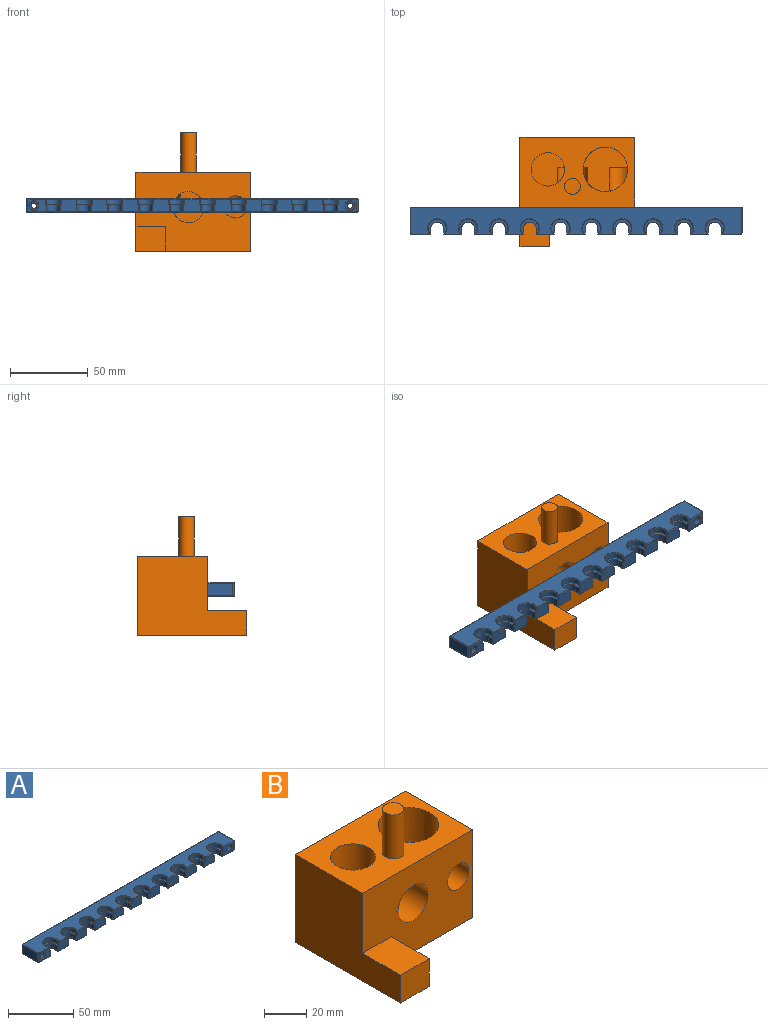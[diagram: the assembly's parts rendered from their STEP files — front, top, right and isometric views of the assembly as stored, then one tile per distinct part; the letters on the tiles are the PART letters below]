
ASSEMBLY  parts=2 mates=1
PART A: 230 faces, bbox 213.6x17.9x8.9 mm
  f0: plane 212.34x16.76mm, normal (0,0,1), area 2525.2mm2, adj f109,f110,f113,f114,f117,f118,f121,f122
  f1: plane 212.34x16.76mm, normal (0,0,-1), area 2906mm2, adj f153,f154,f156,f157,f158,f159,f161,f162
  f2: cylinder r=1.65mm len=9.91mm, axis (0,-1,0), area 102.8mm2, adj f47,f228
  f3: cylinder r=1.65mm len=9.91mm, axis (0,-1,0), area 102.8mm2, adj f47,f229
  f4: plane 4.57x3.56mm, normal (-1,0,0), area 16.3mm2, adj f5,f67,f106,f194
  f5: cylinder r=4.06mm len=8.13mm, axis (0,0,1), area 58.4mm2, adj f4,f6,f67,f192
  f6: plane 4.57x3.56mm, normal (1,0,0), area 16.3mm2, adj f5,f67,f107,f190
  f7: plane 4.57x3.56mm, normal (-1,0,0), area 16.3mm2, adj f8,f65,f104,f182
  f8: cylinder r=4.06mm len=8.13mm, axis (0,0,1), area 58.4mm2, adj f7,f9,f65,f180
  f9: plane 4.57x3.56mm, normal (1,0,0), area 16.3mm2, adj f8,f65,f105,f178
  f10: plane 4.57x3.56mm, normal (-1,0,0), area 16.3mm2, adj f11,f63,f102,f170
  f11: cylinder r=4.06mm len=8.13mm, axis (0,0,1), area 58.4mm2, adj f10,f12,f63,f168
  f12: plane 4.57x3.56mm, normal (1,0,0), area 16.3mm2, adj f11,f63,f103,f166
  f13: plane 4.57x3.56mm, normal (-1,0,0), area 16.3mm2, adj f14,f61,f100,f158
  f14: cylinder r=4.06mm len=8.13mm, axis (0,0,1), area 58.4mm2, adj f13,f15,f61,f156
  f15: plane 4.57x3.56mm, normal (1,0,0), area 16.3mm2, adj f14,f61,f101,f154
  f16: plane 4.57x3.56mm, normal (-1,0,0), area 16.3mm2, adj f17,f59,f98,f157
  f17: cylinder r=4.06mm len=8.13mm, axis (0,0,1), area 58.4mm2, adj f16,f18,f59,f159
  f18: plane 4.57x3.56mm, normal (1,0,0), area 16.3mm2, adj f17,f59,f99,f161
  f19: plane 4.57x3.56mm, normal (-1,0,0), area 16.3mm2, adj f20,f57,f96,f169
  f20: cylinder r=4.06mm len=8.13mm, axis (0,0,1), area 58.4mm2, adj f19,f21,f57,f171
  f21: plane 4.57x3.56mm, normal (1,0,0), area 16.3mm2, adj f20,f57,f97,f173
  f22: plane 4.57x3.56mm, normal (-1,0,0), area 16.3mm2, adj f23,f55,f94,f181
  f23: cylinder r=4.06mm len=8.13mm, axis (0,0,1), area 58.4mm2, adj f22,f24,f55,f183
  f24: plane 4.57x3.56mm, normal (1,0,0), area 16.3mm2, adj f23,f55,f95,f185
  f25: plane 4.57x3.56mm, normal (-1,0,0), area 16.3mm2, adj f26,f53,f92,f193
  f26: cylinder r=4.06mm len=8.13mm, axis (0,0,1), area 58.4mm2, adj f25,f27,f53,f195
  f27: plane 4.57x3.56mm, normal (1,0,0), area 16.3mm2, adj f26,f53,f93,f197
  f28: plane 4.57x3.56mm, normal (-1,0,0), area 16.3mm2, adj f29,f51,f90,f205
  f29: cylinder r=4.06mm len=8.13mm, axis (0,0,1), area 58.4mm2, adj f28,f30,f51,f207
  f30: plane 4.57x3.56mm, normal (1,0,0), area 16.3mm2, adj f29,f51,f91,f209
  f31: plane 4.57x3.56mm, normal (-1,0,0), area 16.3mm2, adj f32,f49,f88,f214
  f32: cylinder r=4.06mm len=8.13mm, axis (0,0,1), area 58.4mm2, adj f31,f33,f49,f212
  f33: plane 4.57x3.56mm, normal (1,0,0), area 16.3mm2, adj f32,f49,f89,f210
  f34: plane 10.67x7.87mm, normal (0,-1,0), area 80.2mm2, adj f49,f51,f85,f86,f88,f91,f134,f213
  f35: plane 10.67x7.87mm, normal (0,-1,0), area 80.2mm2, adj f51,f53,f83,f84,f90,f93,f126,f201
  f36: plane 10.67x7.87mm, normal (0,-1,0), area 80.2mm2, adj f53,f55,f81,f82,f92,f95,f118,f189
  f37: plane 10.67x7.87mm, normal (0,-1,0), area 80.2mm2, adj f55,f57,f79,f80,f94,f97,f110,f177
  f38: plane 10.67x7.87mm, normal (0,-1,0), area 80.2mm2, adj f57,f59,f77,f78,f96,f99,f113,f165
  f39: plane 10.67x7.87mm, normal (0,-1,0), area 80.2mm2, adj f59,f61,f75,f76,f98,f101,f121,f153
  f40: plane 10.67x7.87mm, normal (0,-1,0), area 80.2mm2, adj f61,f63,f73,f74,f100,f103,f129,f162
  f41: plane 10.67x7.87mm, normal (0,-1,0), area 80.2mm2, adj f63,f65,f71,f72,f102,f105,f137,f174
  f42: plane 10.67x7.87mm, normal (0,-1,0), area 80.2mm2, adj f65,f67,f69,f70,f104,f107,f145,f186
  f43: plane 11.68x7.87mm, normal (0,-1,0), area 58.4mm2, adj f67,f68,f106,f150,f198,f221,f223
  f44: plane 16.51x7.87mm, normal (-1,0,0), area 130mm2, adj f47,f144,f204,f226
  f45: plane 11.68x7.87mm, normal (0,-1,0), area 58.4mm2, adj f49,f87,f89,f142,f206,f220,f226
  f46: plane 16.51x7.87mm, normal (1,0,0), area 130mm2, adj f47,f148,f200,f223
  f47: plane 213.36x7.87mm, normal (0,1,0), area 1662.9mm2, adj f2,f3,f44,f46,f146,f202
  f48: cylinder r=5.75mm len=11.49mm, axis (0,0,1), area 82.6mm2, adj f49,f86,f87,f138
  f49: plane 11.49x9.81mm, normal (0,0,1), area 35.7mm2, adj f31,f32,f33,f34,f45,f48,f86,f87
  f50: cylinder r=5.75mm len=11.49mm, axis (0,0,1), area 82.6mm2, adj f51,f84,f85,f130
  f51: plane 11.49x9.81mm, normal (0,0,1), area 35.7mm2, adj f28,f29,f30,f34,f35,f50,f84,f85
  f52: cylinder r=5.75mm len=11.49mm, axis (0,0,1), area 82.6mm2, adj f53,f82,f83,f122
  f53: plane 11.49x9.81mm, normal (0,0,1), area 35.7mm2, adj f25,f26,f27,f35,f36,f52,f82,f83
  f54: cylinder r=5.75mm len=11.49mm, axis (0,0,1), area 82.6mm2, adj f55,f80,f81,f114
  f55: plane 11.49x9.81mm, normal (0,0,1), area 35.7mm2, adj f22,f23,f24,f36,f37,f54,f80,f81
  f56: cylinder r=5.75mm len=11.49mm, axis (0,0,1), area 82.6mm2, adj f57,f78,f79,f109
  f57: plane 11.49x9.81mm, normal (0,0,1), area 35.7mm2, adj f19,f20,f21,f37,f38,f56,f78,f79
  f58: cylinder r=5.75mm len=11.49mm, axis (0,0,1), area 82.6mm2, adj f59,f76,f77,f117
  f59: plane 11.49x9.81mm, normal (0,0,1), area 35.7mm2, adj f16,f17,f18,f38,f39,f58,f76,f77
  f60: cylinder r=5.75mm len=11.49mm, axis (0,0,1), area 82.6mm2, adj f61,f74,f75,f125
  f61: plane 11.49x9.81mm, normal (0,0,1), area 35.7mm2, adj f13,f14,f15,f39,f40,f60,f74,f75
  f62: cylinder r=5.75mm len=11.49mm, axis (0,0,1), area 82.6mm2, adj f63,f72,f73,f133
  f63: plane 11.49x9.81mm, normal (0,0,1), area 35.7mm2, adj f10,f11,f12,f40,f41,f62,f72,f73
  f64: cylinder r=5.75mm len=11.49mm, axis (0,0,1), area 82.6mm2, adj f65,f70,f71,f141
  f65: plane 11.49x9.81mm, normal (0,0,1), area 35.7mm2, adj f7,f8,f9,f41,f42,f64,f70,f71
  f66: cylinder r=5.75mm len=11.49mm, axis (0,0,1), area 82.6mm2, adj f67,f68,f69,f149
  f67: plane 11.49x9.81mm, normal (0,0,1), area 35.7mm2, adj f4,f5,f6,f42,f43,f66,f68,f69
  f68: cylinder r=0.51mm len=3.3mm, axis (0,0,1), area 3.6mm2, adj f43,f66,f67,f151
  f69: cylinder r=0.51mm len=3.3mm, axis (0,0,1), area 3.6mm2, adj f42,f66,f67,f147
  f70: cylinder r=0.51mm len=3.3mm, axis (0,0,1), area 3.6mm2, adj f42,f64,f65,f143
  f71: cylinder r=0.51mm len=3.3mm, axis (0,0,1), area 3.6mm2, adj f41,f64,f65,f139
  f72: cylinder r=0.51mm len=3.3mm, axis (0,0,1), area 3.6mm2, adj f41,f62,f63,f135
  f73: cylinder r=0.51mm len=3.3mm, axis (0,0,1), area 3.6mm2, adj f40,f62,f63,f131
  f74: cylinder r=0.51mm len=3.3mm, axis (0,0,1), area 3.6mm2, adj f40,f60,f61,f127
  f75: cylinder r=0.51mm len=3.3mm, axis (0,0,1), area 3.6mm2, adj f39,f60,f61,f123
  f76: cylinder r=0.51mm len=3.3mm, axis (0,0,1), area 3.6mm2, adj f39,f58,f59,f119
  f77: cylinder r=0.51mm len=3.3mm, axis (0,0,1), area 3.6mm2, adj f38,f58,f59,f115
  f78: cylinder r=0.51mm len=3.3mm, axis (0,0,1), area 3.6mm2, adj f38,f56,f57,f111
  f79: cylinder r=0.51mm len=3.3mm, axis (0,0,1), area 3.6mm2, adj f37,f56,f57,f108
  f80: cylinder r=0.51mm len=3.3mm, axis (0,0,1), area 3.6mm2, adj f37,f54,f55,f112
  f81: cylinder r=0.51mm len=3.3mm, axis (0,0,1), area 3.6mm2, adj f36,f54,f55,f116
  f82: cylinder r=0.51mm len=3.3mm, axis (0,0,1), area 3.6mm2, adj f36,f52,f53,f120
  f83: cylinder r=0.51mm len=3.3mm, axis (0,0,1), area 3.6mm2, adj f35,f52,f53,f124
  f84: cylinder r=0.51mm len=3.3mm, axis (0,0,1), area 3.6mm2, adj f35,f50,f51,f128
  f85: cylinder r=0.51mm len=3.3mm, axis (0,0,1), area 3.6mm2, adj f34,f50,f51,f132
  f86: cylinder r=0.51mm len=3.3mm, axis (0,0,1), area 3.6mm2, adj f34,f48,f49,f136
  f87: cylinder r=0.51mm len=3.3mm, axis (0,0,1), area 3.6mm2, adj f45,f48,f49,f140
  f88: cylinder r=0.51mm len=4.57mm, axis (0,0,-1), area 3.6mm2, adj f31,f34,f49,f215
  f89: cylinder r=0.51mm len=4.57mm, axis (0,0,1), area 3.6mm2, adj f33,f45,f49,f208
  f90: cylinder r=0.51mm len=4.57mm, axis (0,0,-1), area 3.6mm2, adj f28,f35,f51,f203
  f91: cylinder r=0.51mm len=4.57mm, axis (0,0,1), area 3.6mm2, adj f30,f34,f51,f211
  f92: cylinder r=0.51mm len=4.57mm, axis (0,0,-1), area 3.6mm2, adj f25,f36,f53,f191
  f93: cylinder r=0.51mm len=4.57mm, axis (0,0,1), area 3.6mm2, adj f27,f35,f53,f199
  f94: cylinder r=0.51mm len=4.57mm, axis (0,0,-1), area 3.6mm2, adj f22,f37,f55,f179
  f95: cylinder r=0.51mm len=4.57mm, axis (0,0,1), area 3.6mm2, adj f24,f36,f55,f187
  f96: cylinder r=0.51mm len=4.57mm, axis (0,0,-1), area 3.6mm2, adj f19,f38,f57,f167
  f97: cylinder r=0.51mm len=4.57mm, axis (0,0,1), area 3.6mm2, adj f21,f37,f57,f175
  f98: cylinder r=0.51mm len=4.57mm, axis (0,0,-1), area 3.6mm2, adj f16,f39,f59,f155
  f99: cylinder r=0.51mm len=4.57mm, axis (0,0,1), area 3.6mm2, adj f18,f38,f59,f163
  f100: cylinder r=0.51mm len=4.57mm, axis (0,0,-1), area 3.6mm2, adj f13,f40,f61,f160
  f101: cylinder r=0.51mm len=4.57mm, axis (0,0,1), area 3.6mm2, adj f15,f39,f61,f152
  f102: cylinder r=0.51mm len=4.57mm, axis (0,0,-1), area 3.6mm2, adj f10,f41,f63,f172
  f103: cylinder r=0.51mm len=4.57mm, axis (0,0,1), area 3.6mm2, adj f12,f40,f63,f164
  f104: cylinder r=0.51mm len=4.57mm, axis (0,0,-1), area 3.6mm2, adj f7,f42,f65,f184
  f105: cylinder r=0.51mm len=4.57mm, axis (0,0,1), area 3.6mm2, adj f9,f41,f65,f176
  f106: cylinder r=0.51mm len=4.57mm, axis (0,0,-1), area 3.6mm2, adj f4,f43,f67,f196
  f107: cylinder r=0.51mm len=4.57mm, axis (0,0,1), area 3.6mm2, adj f6,f42,f67,f188
  f108: sphere r=0.51mm, area 0.6mm2, adj f79,f109,f110
  f109: torus R=6.26mm, axis (0,0,1), area 20.6mm2, adj f0,f56,f108,f111
  f110: cylinder r=0.51mm len=9.52mm, axis (-1,0,0), area 7.6mm2, adj f0,f37,f108,f112
  f111: sphere r=0.51mm, area 0.6mm2, adj f78,f109,f113
  f112: sphere r=0.51mm, area 0.6mm2, adj f80,f110,f114
  f113: cylinder r=0.51mm len=9.52mm, axis (-1,0,0), area 7.6mm2, adj f0,f38,f111,f115
  f114: torus R=6.26mm, axis (0,0,1), area 20.6mm2, adj f0,f54,f112,f116
  f115: sphere r=0.51mm, area 0.6mm2, adj f77,f113,f117
  f116: sphere r=0.51mm, area 0.6mm2, adj f81,f114,f118
  f117: torus R=6.26mm, axis (0,0,1), area 20.6mm2, adj f0,f58,f115,f119
  f118: cylinder r=0.51mm len=9.52mm, axis (-1,0,0), area 7.6mm2, adj f0,f36,f116,f120
  f119: sphere r=0.51mm, area 0.6mm2, adj f76,f117,f121
  f120: sphere r=0.51mm, area 0.6mm2, adj f82,f118,f122
  f121: cylinder r=0.51mm len=9.52mm, axis (-1,0,0), area 7.6mm2, adj f0,f39,f119,f123
  f122: torus R=6.26mm, axis (0,0,1), area 20.6mm2, adj f0,f52,f120,f124
  f123: sphere r=0.51mm, area 0.6mm2, adj f75,f121,f125
  f124: sphere r=0.51mm, area 0.6mm2, adj f83,f122,f126
  f125: torus R=6.26mm, axis (0,0,1), area 20.6mm2, adj f0,f60,f123,f127
  f126: cylinder r=0.51mm len=9.52mm, axis (-1,0,0), area 7.6mm2, adj f0,f35,f124,f128
  f127: sphere r=0.51mm, area 0.6mm2, adj f74,f125,f129
  f128: sphere r=0.51mm, area 0.6mm2, adj f84,f126,f130
  f129: cylinder r=0.51mm len=9.52mm, axis (-1,0,0), area 7.6mm2, adj f0,f40,f127,f131
  f130: torus R=6.26mm, axis (0,0,1), area 20.6mm2, adj f0,f50,f128,f132
  f131: sphere r=0.51mm, area 0.6mm2, adj f73,f129,f133
  f132: sphere r=0.51mm, area 0.6mm2, adj f85,f130,f134
  f133: torus R=6.26mm, axis (0,0,1), area 20.6mm2, adj f0,f62,f131,f135
  f134: cylinder r=0.51mm len=9.52mm, axis (-1,0,0), area 7.6mm2, adj f0,f34,f132,f136
  f135: sphere r=0.51mm, area 0.6mm2, adj f72,f133,f137
  f136: sphere r=0.51mm, area 0.6mm2, adj f86,f134,f138
  f137: cylinder r=0.51mm len=9.52mm, axis (-1,0,0), area 7.6mm2, adj f0,f41,f135,f139
  f138: torus R=6.26mm, axis (0,0,1), area 20.6mm2, adj f0,f48,f136,f140
  f139: sphere r=0.51mm, area 0.6mm2, adj f71,f137,f141
  f140: sphere r=0.51mm, area 0.6mm2, adj f87,f138,f142
  f141: torus R=6.26mm, axis (0,0,1), area 20.6mm2, adj f0,f64,f139,f143
  f142: cylinder r=0.51mm len=11.11mm, axis (-1,0,0), area 8.9mm2, adj f0,f45,f140,f225
  f143: sphere r=0.51mm, area 0.6mm2, adj f70,f141,f145
  f144: cylinder r=0.51mm len=16.51mm, axis (0,1,0), area 13mm2, adj f0,f44,f146,f225
  f145: cylinder r=0.51mm len=9.52mm, axis (-1,0,0), area 7.6mm2, adj f0,f42,f143,f147
  f146: cylinder r=0.51mm len=213.36mm, axis (1,0,0), area 170mm2, adj f0,f47,f144,f148
  f147: sphere r=0.51mm, area 0.6mm2, adj f69,f145,f149
  f148: cylinder r=0.51mm len=16.51mm, axis (0,-1,0), area 13mm2, adj f0,f46,f146,f222
  f149: torus R=6.26mm, axis (0,0,1), area 20.6mm2, adj f0,f66,f147,f151
  f150: cylinder r=0.51mm len=11.11mm, axis (-1,0,0), area 8.9mm2, adj f0,f43,f151,f222
  f151: sphere r=0.51mm, area 0.6mm2, adj f68,f149,f150
  f152: sphere r=0.51mm, area 0.4mm2, adj f101,f153,f154
  f153: cylinder r=0.51mm len=10.67mm, axis (1,0,0), area 8.5mm2, adj f1,f39,f152,f155
  f154: cylinder r=0.51mm len=3.56mm, axis (0,-1,0), area 2.8mm2, adj f1,f15,f152,f156
  f155: sphere r=0.51mm, area 0.4mm2, adj f98,f153,f157
  f156: torus R=4.57mm, axis (0,0,1), area 10.7mm2, adj f1,f14,f154,f158
  f157: cylinder r=0.51mm len=3.56mm, axis (0,1,0), area 2.8mm2, adj f1,f16,f155,f159
  f158: cylinder r=0.51mm len=3.56mm, axis (0,1,0), area 2.8mm2, adj f1,f13,f156,f160
  f159: torus R=4.57mm, axis (0,0,1), area 10.7mm2, adj f1,f17,f157,f161
  f160: sphere r=0.51mm, area 0.4mm2, adj f100,f158,f162
  f161: cylinder r=0.51mm len=3.56mm, axis (0,-1,0), area 2.8mm2, adj f1,f18,f159,f163
  f162: cylinder r=0.51mm len=10.67mm, axis (1,0,0), area 8.5mm2, adj f1,f40,f160,f164
  f163: sphere r=0.51mm, area 0.4mm2, adj f99,f161,f165
  f164: sphere r=0.51mm, area 0.4mm2, adj f103,f162,f166
  f165: cylinder r=0.51mm len=10.67mm, axis (1,0,0), area 8.5mm2, adj f1,f38,f163,f167
  f166: cylinder r=0.51mm len=3.56mm, axis (0,-1,0), area 2.8mm2, adj f1,f12,f164,f168
  f167: sphere r=0.51mm, area 0.4mm2, adj f96,f165,f169
  f168: torus R=4.57mm, axis (0,0,1), area 10.7mm2, adj f1,f11,f166,f170
  f169: cylinder r=0.51mm len=3.56mm, axis (0,1,0), area 2.8mm2, adj f1,f19,f167,f171
  f170: cylinder r=0.51mm len=3.56mm, axis (0,1,0), area 2.8mm2, adj f1,f10,f168,f172
  f171: torus R=4.57mm, axis (0,0,1), area 10.7mm2, adj f1,f20,f169,f173
  f172: sphere r=0.51mm, area 0.4mm2, adj f102,f170,f174
  f173: cylinder r=0.51mm len=3.56mm, axis (0,-1,0), area 2.8mm2, adj f1,f21,f171,f175
  f174: cylinder r=0.51mm len=10.67mm, axis (1,0,0), area 8.5mm2, adj f1,f41,f172,f176
  f175: sphere r=0.51mm, area 0.4mm2, adj f97,f173,f177
  f176: sphere r=0.51mm, area 0.4mm2, adj f105,f174,f178
  f177: cylinder r=0.51mm len=10.67mm, axis (1,0,0), area 8.5mm2, adj f1,f37,f175,f179
  f178: cylinder r=0.51mm len=3.56mm, axis (0,-1,0), area 2.8mm2, adj f1,f9,f176,f180
  f179: sphere r=0.51mm, area 0.4mm2, adj f94,f177,f181
  f180: torus R=4.57mm, axis (0,0,1), area 10.7mm2, adj f1,f8,f178,f182
  f181: cylinder r=0.51mm len=3.56mm, axis (0,1,0), area 2.8mm2, adj f1,f22,f179,f183
  f182: cylinder r=0.51mm len=3.56mm, axis (0,1,0), area 2.8mm2, adj f1,f7,f180,f184
  f183: torus R=4.57mm, axis (0,0,1), area 10.7mm2, adj f1,f23,f181,f185
  f184: sphere r=0.51mm, area 0.4mm2, adj f104,f182,f186
  f185: cylinder r=0.51mm len=3.56mm, axis (0,-1,0), area 2.8mm2, adj f1,f24,f183,f187
  f186: cylinder r=0.51mm len=10.67mm, axis (1,0,0), area 8.5mm2, adj f1,f42,f184,f188
  f187: sphere r=0.51mm, area 0.4mm2, adj f95,f185,f189
  f188: sphere r=0.51mm, area 0.4mm2, adj f107,f186,f190
  f189: cylinder r=0.51mm len=10.67mm, axis (1,0,0), area 8.5mm2, adj f1,f36,f187,f191
  f190: cylinder r=0.51mm len=3.56mm, axis (0,-1,0), area 2.8mm2, adj f1,f6,f188,f192
  f191: sphere r=0.51mm, area 0.4mm2, adj f92,f189,f193
  f192: torus R=4.57mm, axis (0,0,1), area 10.7mm2, adj f1,f5,f190,f194
  f193: cylinder r=0.51mm len=3.56mm, axis (0,1,0), area 2.8mm2, adj f1,f25,f191,f195
  f194: cylinder r=0.51mm len=3.56mm, axis (0,1,0), area 2.8mm2, adj f1,f4,f192,f196
  f195: torus R=4.57mm, axis (0,0,1), area 10.7mm2, adj f1,f26,f193,f197
  f196: sphere r=0.51mm, area 0.4mm2, adj f106,f194,f198
  f197: cylinder r=0.51mm len=3.56mm, axis (0,-1,0), area 2.8mm2, adj f1,f27,f195,f199
  f198: cylinder r=0.51mm len=11.68mm, axis (1,0,0), area 9.3mm2, adj f1,f43,f196,f224
  f199: sphere r=0.51mm, area 0.4mm2, adj f93,f197,f201
  f200: cylinder r=0.51mm len=16.51mm, axis (0,1,0), area 13mm2, adj f1,f46,f202,f224
  f201: cylinder r=0.51mm len=10.67mm, axis (1,0,0), area 8.5mm2, adj f1,f35,f199,f203
  f202: cylinder r=0.51mm len=213.36mm, axis (-1,0,0), area 170mm2, adj f1,f47,f200,f204
  f203: sphere r=0.51mm, area 0.4mm2, adj f90,f201,f205
  f204: cylinder r=0.51mm len=16.51mm, axis (0,-1,0), area 13mm2, adj f1,f44,f202,f227
  f205: cylinder r=0.51mm len=3.56mm, axis (0,1,0), area 2.8mm2, adj f1,f28,f203,f207
  f206: cylinder r=0.51mm len=11.68mm, axis (1,0,0), area 9.3mm2, adj f1,f45,f208,f227
  f207: torus R=4.57mm, axis (0,0,1), area 10.7mm2, adj f1,f29,f205,f209
  f208: sphere r=0.51mm, area 0.4mm2, adj f89,f206,f210
  f209: cylinder r=0.51mm len=3.56mm, axis (0,-1,0), area 2.8mm2, adj f1,f30,f207,f211
  f210: cylinder r=0.51mm len=3.56mm, axis (0,-1,0), area 2.8mm2, adj f1,f33,f208,f212
  f211: sphere r=0.51mm, area 0.4mm2, adj f91,f209,f213
  f212: torus R=4.57mm, axis (0,0,1), area 10.7mm2, adj f1,f32,f210,f214
  f213: cylinder r=0.51mm len=10.67mm, axis (1,0,0), area 8.5mm2, adj f1,f34,f211,f215
  f214: cylinder r=0.51mm len=3.56mm, axis (0,1,0), area 2.8mm2, adj f1,f31,f212,f215
  f215: sphere r=0.51mm, area 0.4mm2, adj f88,f213,f214
  f216: plane 5.84x5.84mm, normal (0,-1,0), area 15.4mm2, adj f217,f229
  f217: cylinder r=2.92mm len=7.37mm, axis (0,-1,0), area 135.2mm2, adj f216,f221
  f218: plane 5.84x5.84mm, normal (0,-1,0), area 15.4mm2, adj f219,f228
  f219: cylinder r=2.92mm len=7.37mm, axis (0,-1,0), area 135.2mm2, adj f218,f220
  f220: torus R=3.17mm, axis (0,1,0), area 7.6mm2, adj f45,f219
  f221: torus R=3.17mm, axis (0,1,0), area 7.6mm2, adj f43,f217
  f222: torus R=0.76mm, axis (0,0,1), area 1.4mm2, adj f0,f148,f150,f223
  f223: cylinder r=1.27mm len=7.87mm, axis (0,0,1), area 15.7mm2, adj f43,f46,f222,f224
  f224: torus R=0.76mm, axis (0,0,1), area 1.4mm2, adj f1,f198,f200,f223
  f225: torus R=0.76mm, axis (0,0,1), area 1.4mm2, adj f0,f142,f144,f226
  f226: cylinder r=1.27mm len=7.87mm, axis (0,0,-1), area 15.7mm2, adj f44,f45,f225,f227
  f227: torus R=0.76mm, axis (0,0,1), area 1.4mm2, adj f1,f204,f206,f226
  f228: torus R=1.91mm, axis (0,-1,0), area 4.4mm2, adj f2,f218
  f229: torus R=1.91mm, axis (0,-1,0), area 4.4mm2, adj f3,f216
PART B: 19 faces, bbox 73.6x70.3x76.2 mm
  f0: plane 70.28x50.8mm, normal (-1,0,0), area 2687.6mm2, adj f1,f3,f4,f5,f17,f18
  f1: plane 73.62x50.8mm, normal (0,-1,0), area 2951.3mm2, adj f0,f2,f4,f5,f12,f14,f16,f17
  f2: plane 50.8x44.88mm, normal (1,0,0), area 2279.9mm2, adj f1,f3,f4,f5
  f3: plane 73.62x50.8mm, normal (0,1,0), area 3739.7mm2, adj f0,f2,f4,f5
  f4: plane 73.62x44.88mm, normal (0,0,1), area 2217.8mm2, adj f0,f1,f2,f3,f6,f8,f10
  f5: plane 73.62x70.28mm, normal (0,0,-1), area 3793.3mm2, adj f0,f1,f2,f3,f16,f18
  f6: cylinder r=14.32mm len=28.63mm, axis (0,0,1), area 1991.7mm2, adj f4,f7,f12,f13,f14,f15
  f7: plane 28.63x28.54mm, normal (0,0,1), area 487.6mm2, adj f6,f12,f13,f14,f15
  f8: cylinder r=10.72mm len=25.4mm, axis (0,0,1), area 1592.9mm2, adj f4,f9,f12,f13
  f9: plane 21.45x21.38mm, normal (0,0,1), area 329.1mm2, adj f8,f12,f13
  f10: cylinder r=5.08mm len=25.4mm, axis (0,0,-1), area 810.7mm2, adj f4,f11
  f11: plane 10.16x10.16mm, normal (0,0,1), area 81.1mm2, adj f10
  f12: cylinder r=10.06mm len=25.4mm, axis (0,-1,0), area 1389.1mm2, adj f1,f6,f7,f8,f9,f13
  f13: plane 20.12x19.24mm, normal (0,-1,0), area 249.6mm2, adj f6,f7,f8,f9,f12
  f14: cylinder r=7.16mm len=25.4mm, axis (0,-1,0), area 880.7mm2, adj f1,f6,f7,f15
  f15: plane 13.61x12.13mm, normal (0,-1,0), area 49.7mm2, adj f6,f7,f14
  f16: plane 25.4x16.05mm, normal (1,0,0), area 407.6mm2, adj f1,f5,f17,f18
  f17: plane 25.4x19.27mm, normal (0,0,1), area 489.4mm2, adj f0,f1,f16,f18
  f18: plane 19.27x16.05mm, normal (0,-1,0), area 309.2mm2, adj f0,f5,f16,f17
PLACE A t=(5.56,-27.03,24.84)mm
PLACE B t=(0,-14.81,0)mm
MATE planar A.f47 <-> B.f1  axis (0,1,0) through (2.24,-39.05,29.29)mm
